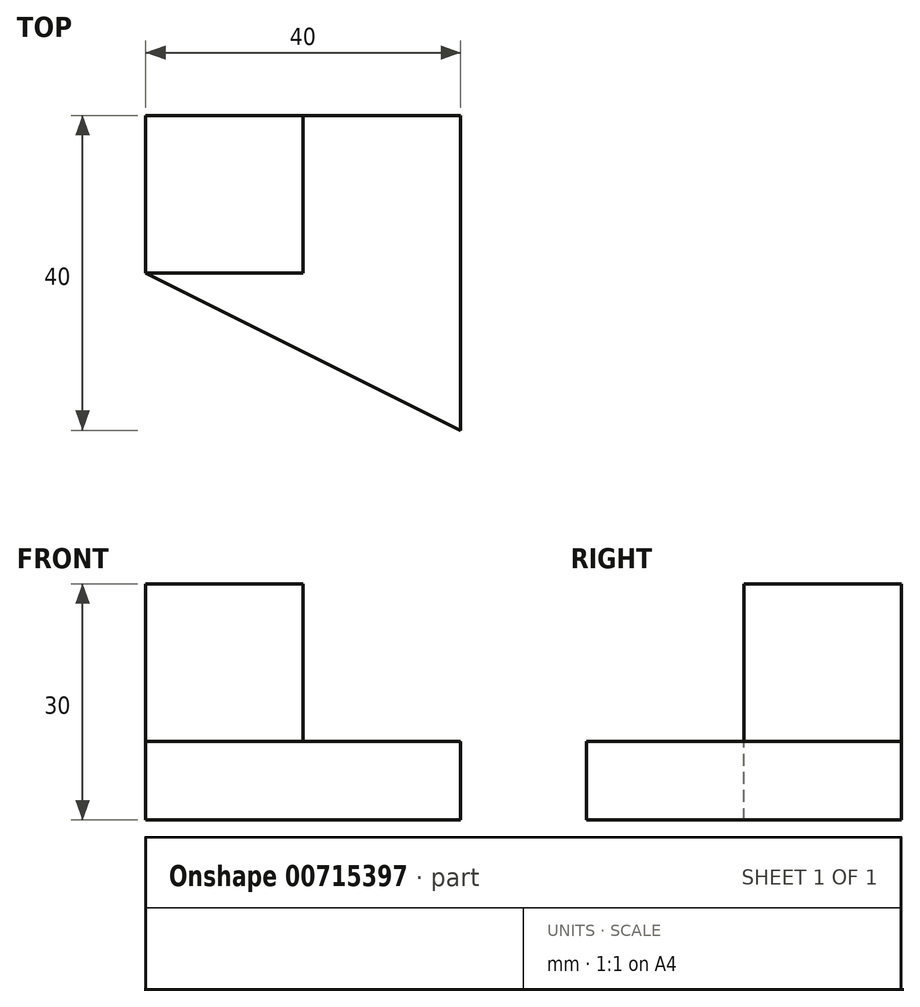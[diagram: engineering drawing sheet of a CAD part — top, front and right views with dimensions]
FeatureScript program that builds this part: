
annotation { "Feature Type Name" : "Feature", "Feature Type Description" : "" }
export const myFeature = defineFeature(function(context is Context, id is Id, definition is map)
    precondition{}
    {
        {
            var Q0;
            Q0=qCreatedBy(makeId("Front.planeOp"),FACE);
            var sketch = newSketch(context, id + "F0", { "sketchPlane" : qUnion([Q0])});
            skLineSegment(sketch, "E0", {"start": v(0, 0) * mm, "end": v(40, 0) * mm});
            skLineSegment(sketch, "E1", {"start": v(40, 0) * mm, "end": v(40, 30) * mm});
            skLineSegment(sketch, "E2", {"start": v(40, 30) * mm, "end": v(0, 30) * mm});
            skLineSegment(sketch, "E3", {"start": v(0, 30) * mm, "end": v(0, 0) * mm});
            skSolve(sketch);
        }
        {
            var Q0;
            Q0=makeQuery(id+"F0.imprint","IMPRINT",FACE,{"disambiguationData":[TD([[makeQuery(id+"F0.imprint","IMPRINT",EDGE,{"derivedFrom":sQuery(id+"F0.wireOp",EDGE,"E0")}),1.0]])]});
            extrude(context, id + "F1", {"entities" : qUnion([Q0]), "depth" : 40 * mm, "offsetDistance" : 25 * mm});
        }
        {
            var Q0;
            Q0=makeQuery(id+"F1.opExtrude","SWEPT_FACE",FACE,{"disambiguationData":[OSD([sQuery(id+"F0.wireOp",EDGE,"E2")])]});
            var sketch = newSketch(context, id + "F2", { "sketchPlane" : qUnion([Q0])});
            skLineSegment(sketch, "E4", {"start": v(40, -20) * mm, "end": v(20, -20) * mm});
            skLineSegment(sketch, "E5", {"start": v(20, -20) * mm, "end": v(20, 0) * mm});
            skLineSegment(sketch, "E6", {"start": v(20, 0) * mm, "end": v(40, 0) * mm});
            skLineSegment(sketch, "E7", {"start": v(40, 0) * mm, "end": v(40, -20) * mm});
            skLineSegment(sketch, "E8", {"start": v(20, -20) * mm, "end": v(0, -20) * mm});
            skLineSegment(sketch, "E9", {"start": v(0, -20) * mm, "end": v(40, -20) * mm});
            skLineSegment(sketch, "E10", {"start": v(40, -20) * mm, "end": v(40, -40) * mm});
            skLineSegment(sketch, "E11", {"start": v(40, -40) * mm, "end": v(0, -20) * mm});
            skSolve(sketch);
        }
        {
            var Q0;
            {var subQ0=sQuery(id+"F2.wireOp",EDGE,"E11");Q0=makeQuery(id+"F2.imprint","IMPRINT",FACE,{"disambiguationData":[TD([[makeQuery(id+"F2.imprint","IMPRINT",EDGE,{"derivedFrom":subQ0}),1.0]])]});}
            extrude(context, id + "F3", {"entities" : qUnion([Q0]), "operationType" : NewBodyOperationType.REMOVE, "oppositeDirection" : true, "depth" : 30 * mm, "offsetDistance" : 25 * mm});
        }
        {
            var Q0;
            Q0=makeQuery(id+"F1.opExtrude","SWEPT_FACE",FACE,{"disambiguationData":[OSD([sQuery(id+"F0.wireOp",EDGE,"E2")])]});
            var sketch = newSketch(context, id + "F4", { "sketchPlane" : qUnion([Q0])});
            skLineSegment(sketch, "E12", {"start": v(20, 0) * mm, "end": v(20, -20) * mm});
            skLineSegment(sketch, "E13", {"start": v(20, -20) * mm, "end": v(0, -20) * mm});
            skLineSegment(sketch, "E14", {"start": v(0, -20) * mm, "end": v(40, -40) * mm});
            skLineSegment(sketch, "E15", {"start": v(40, -40) * mm, "end": v(40, 0) * mm});
            skLineSegment(sketch, "E16", {"start": v(40, 0) * mm, "end": v(20, 0) * mm});
            skSolve(sketch);
        }
        {
            var Q0;
            Q0=makeQuery(id+"F4.imprint","IMPRINT",FACE,{"disambiguationData":[TD([[makeQuery(id+"F4.imprint","IMPRINT",EDGE,{"derivedFrom":sQuery(id+"F4.wireOp",EDGE,"E12")}),1.0]])]});
            extrude(context, id + "F5", {"entities" : qUnion([Q0]), "operationType" : NewBodyOperationType.REMOVE, "oppositeDirection" : true, "depth" : 20 * mm, "offsetDistance" : 25 * mm});
        }
    });
